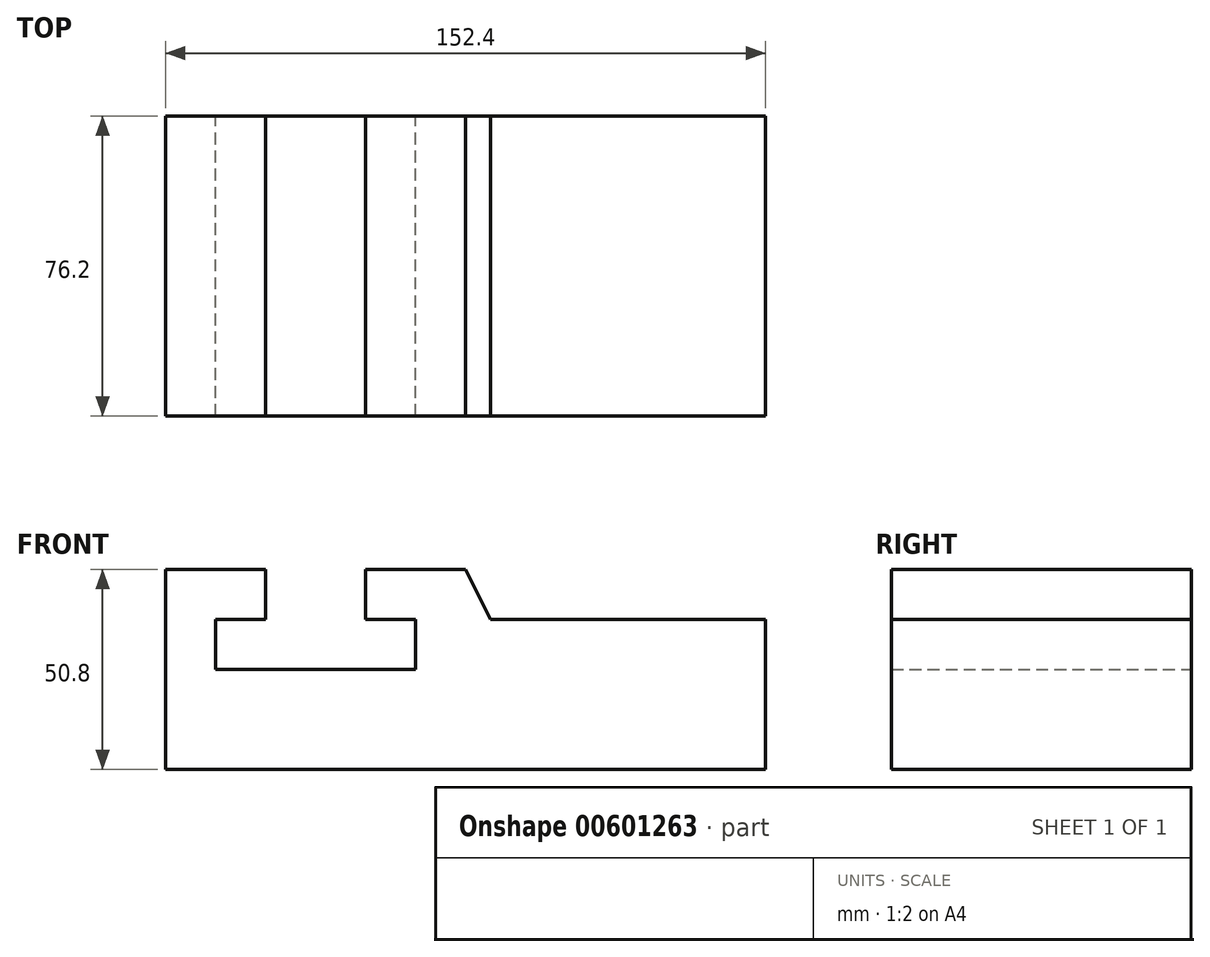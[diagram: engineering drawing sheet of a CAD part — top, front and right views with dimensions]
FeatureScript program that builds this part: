
annotation { "Feature Type Name" : "Feature", "Feature Type Description" : "" }
export const myFeature = defineFeature(function(context is Context, id is Id, definition is map)
    precondition{}
    {
        {
            var Q0;
            Q0=qCreatedBy(makeId("Front.planeOp"),FACE);
            var sketch = newSketch(context, id + "F0", { "sketchPlane" : qUnion([Q0])});
            skLineSegment(sketch, "E0", {"start": v(0, 0) * mm, "end": v(152.4, 0) * mm});
            skLineSegment(sketch, "E1", {"start": v(0, 0) * mm, "end": v(0, 50.8) * mm});
            skLineSegment(sketch, "E2", {"start": v(0, 50.8) * mm, "end": v(25.4, 50.8) * mm});
            skLineSegment(sketch, "E3", {"start": v(25.4, 50.8) * mm, "end": v(25.4, 38.1) * mm});
            skLineSegment(sketch, "E4", {"start": v(25.4, 38.1) * mm, "end": v(12.7, 38.1) * mm});
            skPoint(sketch, "E4.endSnap0", {"position": v(12.7, 50.8) * mm});
            skLineSegment(sketch, "E5", {"start": v(12.7, 38.1) * mm, "end": v(12.7, 25.4) * mm});
            skLineSegment(sketch, "E6", {"start": v(12.7, 25.4) * mm, "end": v(63.5, 25.4) * mm});
            skLineSegment(sketch, "E7", {"start": v(63.5, 25.4) * mm, "end": v(63.5, 38.1) * mm});
            skLineSegment(sketch, "E8", {"start": v(63.5, 38.1) * mm, "end": v(50.8, 38.1) * mm});
            skLineSegment(sketch, "E9", {"start": v(50.8, 38.1) * mm, "end": v(50.8, 50.8) * mm});
            skLineSegment(sketch, "E10", {"start": v(50.8, 50.8) * mm, "end": v(76.2, 50.8) * mm});
            skLineSegment(sketch, "E11", {"start": v(152.4, 0) * mm, "end": v(152.4, 38.1) * mm});
            skLineSegment(sketch, "E12", {"start": v(82.55, 38.1) * mm, "end": v(76.2, 50.8) * mm});
            skLineSegment(sketch, "E13", {"start": v(82.55, 38.1) * mm, "end": v(152.4, 38.1) * mm});
            skSolve(sketch);
        }
        {
            var Q0;
            Q0=makeQuery(id+"F0.imprint","IMPRINT",FACE,{"disambiguationData":[TD([[makeQuery(id+"F0.imprint","IMPRINT",EDGE,{"derivedFrom":sQuery(id+"F0.wireOp",EDGE,"E0")}),1.0]])]});
            extrude(context, id + "F1", {"entities" : qUnion([Q0]), "depth" : 76.2 * mm, "offsetDistance" : 25.4 * mm});
        }
    });
